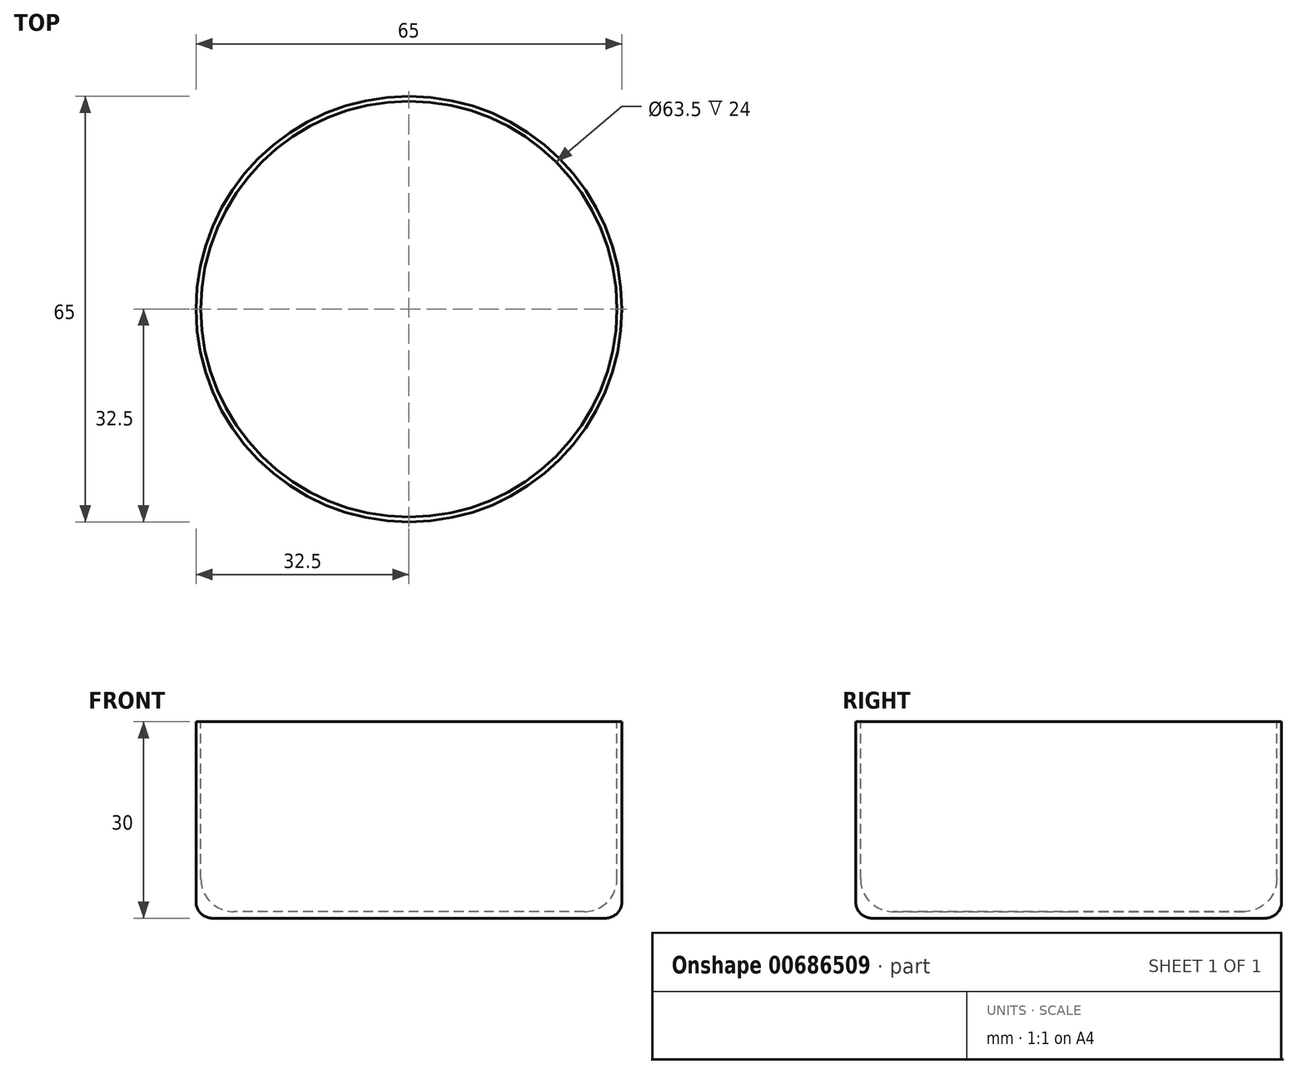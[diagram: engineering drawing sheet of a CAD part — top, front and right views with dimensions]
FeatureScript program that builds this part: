
annotation { "Feature Type Name" : "Feature", "Feature Type Description" : "" }
export const myFeature = defineFeature(function(context is Context, id is Id, definition is map)
    precondition{}
    {
        {
            var Q0;
            Q0=qCreatedBy(makeId("Top.planeOp"),FACE);
            var sketch = newSketch(context, id + "F0", { "sketchPlane" : qUnion([Q0])});
            skCircle(sketch, "E0", {"center": v(0, 0) * mm, "radius": 32.5 * mm});
            skSolve(sketch);
        }
        {
            var Q0;
            Q0=makeQuery(id+"F0.imprint","IMPRINT",FACE,{"disambiguationData":[TD([[makeQuery(id+"F0.imprint","IMPRINT",EDGE,{"derivedFrom":sQuery(id+"F0.wireOp",EDGE,"E0")}),1.0]])]});
            extrude(context, id + "F1", {"entities" : qUnion([Q0]), "depth" : 30 * mm, "offsetDistance" : 25 * mm});
        }
        {
            var Q0;
            Q0=makeQuery(id+"F1.opExtrude","CAP_FACE",FACE,{"disambiguationData":[OSD([sQuery(id+"F0.wireOp",EDGE,"E0")])],"isStart":false});
            var sketch = newSketch(context, id + "F2", { "sketchPlane" : qUnion([Q0])});
            skCircle(sketch, "E1", {"center": v(0, 0) * mm, "radius": 31.75 * mm});
            skSolve(sketch);
        }
        {
            var Q0;
            Q0=makeQuery(id+"F2.imprint","IMPRINT",FACE,{"disambiguationData":[TD([[makeQuery(id+"F2.imprint","IMPRINT",EDGE,{"derivedFrom":sQuery(id+"F2.wireOp",EDGE,"E1")}),1.0]])]});
            extrude(context, id + "F3", {"entities" : qUnion([Q0]), "operationType" : NewBodyOperationType.REMOVE, "oppositeDirection" : true, "depth" : 29 * mm, "offsetDistance" : 25 * mm});
        }
        {
            var Q0;
            Q0=makeQuery(id+"F3.boolean.opBoolean","COPY",EDGE,{"derivedFrom":makeQuery(id+"F3.opExtrude","CAP_EDGE",EDGE,{"disambiguationData":[OSD([sQuery(id+"F2.wireOp",EDGE,"E1")])],"isStart":false})});
            fillet(context, id + "F4", {"entities" : qUnion([Q0]), "radius" : 5 * mm, "tangentPropagation" : true, "allowEdgeOverflow" : false});
        }
        {
            var Q0;
            Q0=makeQuery(id+"F1.opExtrude","CAP_FACE",FACE,{"disambiguationData":[OSD([sQuery(id+"F0.wireOp",EDGE,"E0")])],"isStart":true});
            fillet(context, id + "F5", {"entities" : qUnion([Q0]), "radius" : 2.5 * mm, "tangentPropagation" : true, "allowEdgeOverflow" : false});
        }
    });
